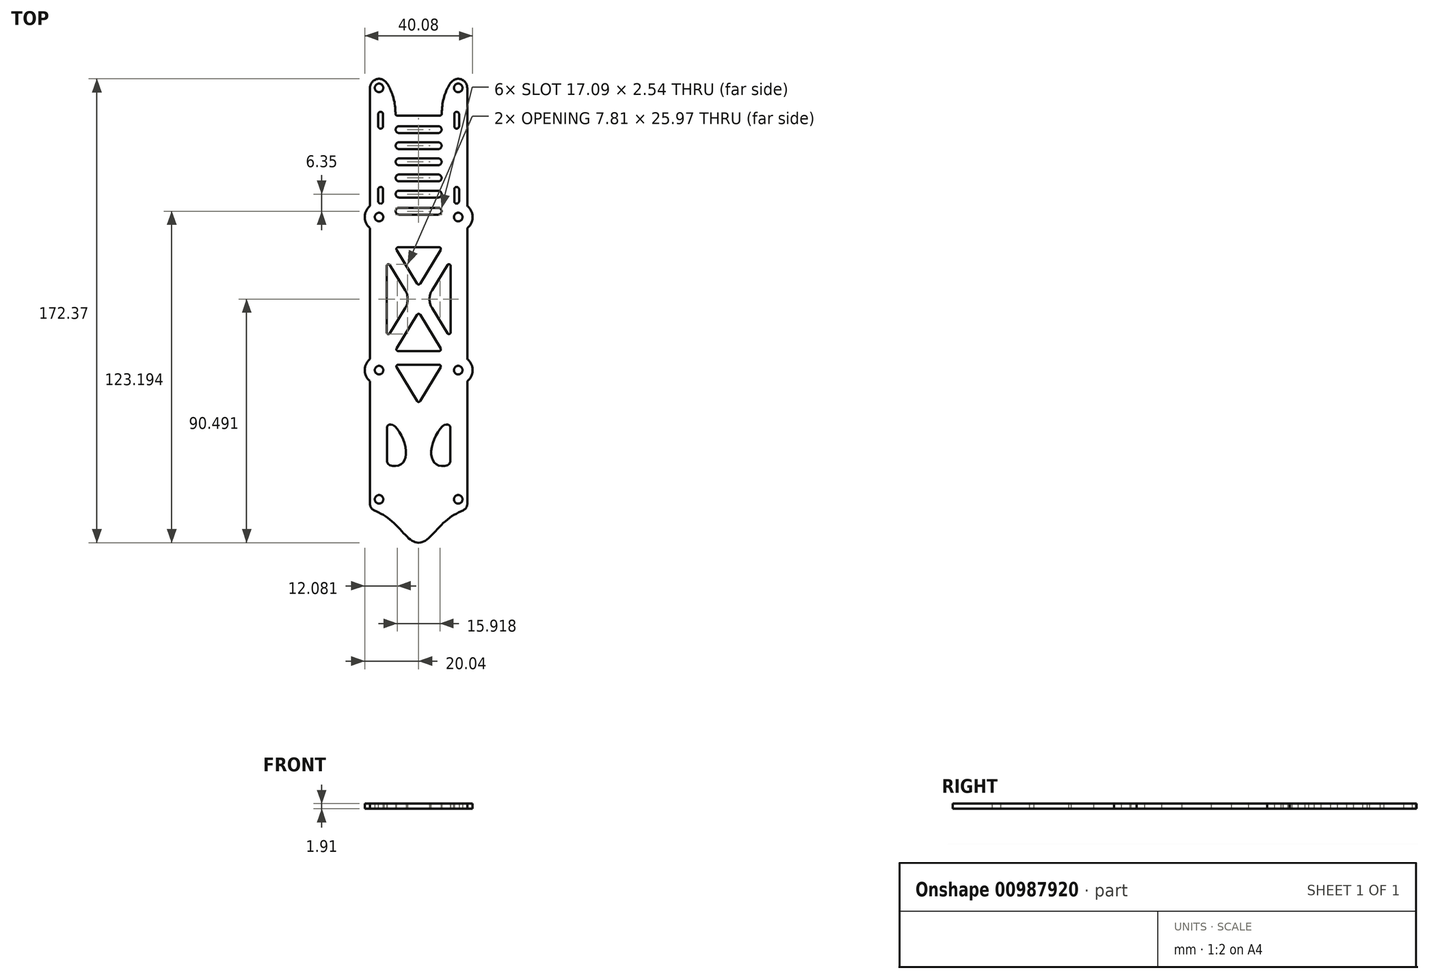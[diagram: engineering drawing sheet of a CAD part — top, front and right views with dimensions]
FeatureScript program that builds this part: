
annotation { "Feature Type Name" : "Feature", "Feature Type Description" : "" }
export const myFeature = defineFeature(function(context is Context, id is Id, definition is map)
    precondition{}
    {
        {
            var Q0;
            Q0=qCreatedBy(makeId("Top.planeOp"),FACE);
            var sketch = newSketch(context, id + "F0", { "sketchPlane" : qUnion([Q0])});
            skLineSegment(sketch, "E0.bottom", {"start": v(-8.07, 64.3) * mm, "end": v(0, 64.3) * mm});
            skLineSegment(sketch, "E0.left", {"start": v(-18.06, 64.3) * mm, "end": v(-18.06, 30.7) * mm});
            skLineSegment(sketch, "E1", {"start": v(-18.06, 64.3) * mm, "end": v(-18.06, 74.56) * mm});
            skArc(sketch, "E2", {"start": v(-12.9, 77.38) * mm, "mid": v(-16.31, 77.5) * mm, "end": v(-18.06, 74.56) * mm});
            skFitSpline(sketch, "E3", {"points": [v(-12.9, 77.38) * mm, v(-10.75, 74.43) * mm, v(-9.09, 69.74) * mm, v(-8.56, 64.3) * mm], "startDerivative": vector(10.32, -7.55) * mm, "endDerivative": vector(0.35, -10.82) * mm});
            skArc(sketch, "E4.filletArc", {"start": v(-8.58, 64.78) * mm, "mid": v(-8.42, 64.44) * mm, "end": v(-8.07, 64.3) * mm});
            skLineSegment(sketch, "E5", {"start": v(0, -94.46) * mm, "end": v(0, 99.76) * mm, "construction": true});
            skCircle(sketch, "E6", {"center": v(-14.7, 26.55) * mm, "radius": 1.59 * mm});
            skCircle(sketch, "E7", {"center": v(-14.7, -30.34) * mm, "radius": 1.59 * mm});
            skPoint(sketch, "E8.visualSharp", {"position": v(-18.06, -81.76) * mm});
            skCircle(sketch, "E9", {"center": v(-14.7, -78.35) * mm, "radius": 1.59 * mm});
            skFitSpline(sketch, "E10", {"points": [v(-18.06, -81.76) * mm, v(-10.46, -86.04) * mm, v(-3.87, -92.63) * mm, v(0, -94.46) * mm], "startDerivative": vector(21.5, -9.36) * mm, "endDerivative": vector(16.7, 0) * mm});
            skArc(sketch, "E11.filletArc", {"start": v(-18.06, -80.1) * mm, "mid": v(-17.65, -81.48) * mm, "end": v(-16.57, -82.42) * mm});
            skCircle(sketch, "E12", {"center": v(-14.7, 74.56) * mm, "radius": 1.59 * mm});
            skLineSegment(sketch, "E13.MirrorCS", {"start": v(8.07, 64.3) * mm, "end": v(0, 64.3) * mm});
            skArc(sketch, "E14.MirrorCS", {"start": v(8.58, 64.78) * mm, "mid": v(8.42, 64.44) * mm, "end": v(8.07, 64.3) * mm});
            skFitSpline(sketch, "E15.MirrorCS", {"points": [v(12.9, 77.38) * mm, v(10.75, 74.43) * mm, v(9.09, 69.74) * mm, v(8.56, 64.3) * mm], "startDerivative": vector(-10.32, -7.55) * mm, "endDerivative": vector(-0.35, -10.82) * mm});
            skArc(sketch, "E16.MirrorCS", {"start": v(12.9, 77.38) * mm, "mid": v(16.31, 77.5) * mm, "end": v(18.06, 74.56) * mm});
            skCircle(sketch, "E17.MirrorC", {"center": v(14.7, 74.56) * mm, "radius": 1.59 * mm});
            skLineSegment(sketch, "E18.MirrorCS", {"start": v(18.06, 64.3) * mm, "end": v(18.06, 74.56) * mm});
            skLineSegment(sketch, "E19.MirrorCS", {"start": v(18.06, 64.3) * mm, "end": v(18.06, 30.7) * mm});
            skCircle(sketch, "E20.MirrorC", {"center": v(14.7, 26.55) * mm, "radius": 1.59 * mm});
            skCircle(sketch, "E21.MirrorC", {"center": v(14.7, -30.34) * mm, "radius": 1.59 * mm});
            skCircle(sketch, "E22.MirrorC", {"center": v(14.7, -78.35) * mm, "radius": 1.59 * mm});
            skArc(sketch, "E23.MirrorCS", {"start": v(18.06, -80.1) * mm, "mid": v(17.65, -81.48) * mm, "end": v(16.57, -82.42) * mm});
            skFitSpline(sketch, "E24.MirrorCS", {"points": [v(18.06, -81.76) * mm, v(10.46, -86.04) * mm, v(3.87, -92.63) * mm, v(0, -94.46) * mm], "startDerivative": vector(-21.5, -9.36) * mm, "endDerivative": vector(-16.7, 0) * mm});
            skLineSegment(sketch, "E25", {"start": v(-11.86, 8.38) * mm, "end": v(-11.86, -16.32) * mm});
            skLineSegment(sketch, "E26", {"start": v(-10.7, -16.65) * mm, "end": v(-4.98, -7.27) * mm});
            skLineSegment(sketch, "E27", {"start": v(-4.98, -0.67) * mm, "end": v(-10.7, 8.71) * mm});
            skLineSegment(sketch, "E28", {"start": v(-0.54, -9.74) * mm, "end": v(-8.18, -22.3) * mm});
            skLineSegment(sketch, "E29", {"start": v(-7.64, -23.25) * mm, "end": v(0, -23.25) * mm});
            skLineSegment(sketch, "E30", {"start": v(-2.97, -3.97) * mm, "end": v(7.15, -3.97) * mm, "construction": true});
            skLineSegment(sketch, "E31.MirrorCS", {"start": v(-0.54, 1.8) * mm, "end": v(-8.18, 14.36) * mm});
            skLineSegment(sketch, "E32.MirrorCS", {"start": v(-7.64, 15.32) * mm, "end": v(0, 15.32) * mm});
            skPoint(sketch, "E33.visualSharp", {"position": v(-2.97, -3.97) * mm});
            skArc(sketch, "E33.filletArc", {"start": v(-4.98, -7.27) * mm, "mid": v(-4.06, -3.97) * mm, "end": v(-4.98, -0.67) * mm});
            skPoint(sketch, "E34.visualSharp", {"position": v(-11.86, 10.64) * mm});
            skArc(sketch, "E34.filletArc", {"start": v(-10.7, 8.71) * mm, "mid": v(-11.4, 9) * mm, "end": v(-11.86, 8.38) * mm});
            skPoint(sketch, "E35.visualSharp", {"position": v(-11.86, -18.57) * mm});
            skArc(sketch, "E35.filletArc", {"start": v(-11.86, -16.32) * mm, "mid": v(-11.4, -16.93) * mm, "end": v(-10.7, -16.65) * mm});
            skPoint(sketch, "E36.visualSharp", {"position": v(-8.76, 15.32) * mm});
            skArc(sketch, "E36.filletArc", {"start": v(-7.64, 15.32) * mm, "mid": v(-8.19, 15) * mm, "end": v(-8.18, 14.36) * mm});
            skPoint(sketch, "E37.visualSharp", {"position": v(-8.76, -23.25) * mm});
            skArc(sketch, "E37.filletArc", {"start": v(-8.18, -22.3) * mm, "mid": v(-8.19, -22.93) * mm, "end": v(-7.64, -23.25) * mm});
            skLineSegment(sketch, "E38.MirrorCS", {"start": v(7.64, 15.32) * mm, "end": v(0, 15.32) * mm});
            skLineSegment(sketch, "E39.MirrorCS", {"start": v(0.54, 1.8) * mm, "end": v(8.18, 14.36) * mm});
            skArc(sketch, "E40.MirrorCS", {"start": v(7.64, 15.32) * mm, "mid": v(8.19, 15) * mm, "end": v(8.18, 14.36) * mm});
            skLineSegment(sketch, "E41.MirrorCS", {"start": v(4.98, -0.67) * mm, "end": v(10.7, 8.71) * mm});
            skLineSegment(sketch, "E42.MirrorCS", {"start": v(11.86, 8.38) * mm, "end": v(11.86, -16.32) * mm});
            skArc(sketch, "E43.MirrorCS", {"start": v(10.7, 8.71) * mm, "mid": v(11.4, 9) * mm, "end": v(11.86, 8.38) * mm});
            skLineSegment(sketch, "E44.MirrorCS", {"start": v(10.7, -16.65) * mm, "end": v(4.98, -7.27) * mm});
            skArc(sketch, "E45.MirrorCS", {"start": v(11.86, -16.32) * mm, "mid": v(11.4, -16.93) * mm, "end": v(10.7, -16.65) * mm});
            skLineSegment(sketch, "E46.MirrorCS", {"start": v(0.54, -9.74) * mm, "end": v(8.18, -22.3) * mm});
            skLineSegment(sketch, "E47.MirrorCS", {"start": v(7.64, -23.25) * mm, "end": v(0, -23.25) * mm});
            skArc(sketch, "E48.MirrorCS", {"start": v(4.98, -7.27) * mm, "mid": v(4.06, -3.97) * mm, "end": v(4.98, -0.67) * mm});
            skArc(sketch, "E49.MirrorCS", {"start": v(8.18, -22.3) * mm, "mid": v(8.19, -22.93) * mm, "end": v(7.64, -23.25) * mm});
            skPoint(sketch, "E50.visualSharp", {"position": v(0, 0.92) * mm});
            skArc(sketch, "E50.filletArc", {"start": v(-0.54, 1.8) * mm, "mid": v(0, 1.5) * mm, "end": v(0.54, 1.8) * mm});
            skPoint(sketch, "E51.visualSharp", {"position": v(0, -8.86) * mm});
            skArc(sketch, "E51.filletArc", {"start": v(0.54, -9.74) * mm, "mid": v(0, -9.44) * mm, "end": v(-0.54, -9.74) * mm});
            skArc(sketch, "E52", {"start": v(-18.06, 30.7) * mm, "mid": v(-20.04, 26.55) * mm, "end": v(-18.06, 22.41) * mm});
            skArc(sketch, "E53", {"start": v(18.06, 22.41) * mm, "mid": v(20.04, 26.55) * mm, "end": v(18.06, 30.7) * mm});
            skArc(sketch, "E54", {"start": v(18.06, -34.48) * mm, "mid": v(20.04, -30.34) * mm, "end": v(18.06, -26.2) * mm});
            skArc(sketch, "E55", {"start": v(-18.06, -26.2) * mm, "mid": v(-20.04, -30.34) * mm, "end": v(-18.06, -34.48) * mm});
            skLineSegment(sketch, "E56.trimOffspring", {"start": v(18.06, -34.48) * mm, "end": v(18.06, -80.1) * mm});
            skLineSegment(sketch, "E57.trimOffspring", {"start": v(-18.06, -34.48) * mm, "end": v(-18.06, -80.1) * mm});
            skLineSegment(sketch, "E58.trimOffspring", {"start": v(18.06, 22.41) * mm, "end": v(18.06, -26.2) * mm});
            skLineSegment(sketch, "E59.trimOffspring", {"start": v(-18.06, 22.41) * mm, "end": v(-18.06, -26.2) * mm});
            skLineSegment(sketch, "E60", {"start": v(-11.72, -64.38) * mm, "end": v(-11.72, -51.49) * mm});
            skFitSpline(sketch, "E61", {"points": [v(-11.72, -51.49) * mm, v(-9.93, -50.58) * mm, v(-4.83, -59.28) * mm, v(-7.13, -65.64) * mm, v(-11.72, -64.38) * mm], "startDerivative": vector(1.58, 12.9) * mm, "endDerivative": vector(-1.26, 20.83) * mm});
            skFitSpline(sketch, "E62.MirrorCS", {"points": [v(11.72, -51.49) * mm, v(9.93, -50.58) * mm, v(4.83, -59.28) * mm, v(7.13, -65.64) * mm, v(11.72, -64.38) * mm], "startDerivative": vector(-1.58, 12.9) * mm, "endDerivative": vector(1.26, 20.83) * mm});
            skLineSegment(sketch, "E63.MirrorCS", {"start": v(11.72, -64.38) * mm, "end": v(11.72, -51.49) * mm});
            skArc(sketch, "E64", {"start": v(-13.23, 64.75) * mm, "mid": v(-14.12, 65.64) * mm, "end": v(-15.01, 64.75) * mm});
            skArc(sketch, "E65", {"start": v(-15.01, 60.3) * mm, "mid": v(-14.12, 59.42) * mm, "end": v(-13.23, 60.3) * mm});
            skArc(sketch, "E66", {"start": v(-13.23, 36.86) * mm, "mid": v(-14.12, 37.75) * mm, "end": v(-15.01, 36.86) * mm});
            skArc(sketch, "E67", {"start": v(-15.01, 32.42) * mm, "mid": v(-14.12, 31.53) * mm, "end": v(-13.23, 32.42) * mm});
            skLineSegment(sketch, "E68", {"start": v(-15.01, 64.75) * mm, "end": v(-15.01, 60.3) * mm});
            skLineSegment(sketch, "E69", {"start": v(-13.23, 64.75) * mm, "end": v(-13.23, 60.3) * mm});
            skLineSegment(sketch, "E70", {"start": v(-15.01, 36.86) * mm, "end": v(-15.01, 32.42) * mm});
            skLineSegment(sketch, "E71", {"start": v(-13.23, 36.86) * mm, "end": v(-13.23, 32.42) * mm});
            skArc(sketch, "E72.MirrorCS", {"start": v(13.23, 64.75) * mm, "mid": v(14.12, 65.64) * mm, "end": v(15.01, 64.75) * mm});
            skLineSegment(sketch, "E73.MirrorCS", {"start": v(15.01, 64.75) * mm, "end": v(15.01, 60.3) * mm});
            skArc(sketch, "E74.MirrorCS", {"start": v(15.01, 60.3) * mm, "mid": v(14.12, 59.42) * mm, "end": v(13.23, 60.3) * mm});
            skLineSegment(sketch, "E75.MirrorCS", {"start": v(13.23, 64.75) * mm, "end": v(13.23, 60.3) * mm});
            skArc(sketch, "E76.MirrorCS", {"start": v(13.23, 36.86) * mm, "mid": v(14.12, 37.75) * mm, "end": v(15.01, 36.86) * mm});
            skLineSegment(sketch, "E77.MirrorCS", {"start": v(15.01, 36.86) * mm, "end": v(15.01, 32.42) * mm});
            skLineSegment(sketch, "E78.MirrorCS", {"start": v(13.23, 36.86) * mm, "end": v(13.23, 32.42) * mm});
            skArc(sketch, "E79.MirrorCS", {"start": v(15.01, 32.42) * mm, "mid": v(14.12, 31.53) * mm, "end": v(13.23, 32.42) * mm});
            skArc(sketch, "E80", {"start": v(-7.28, 36.35) * mm, "mid": v(-8.55, 35.08) * mm, "end": v(-7.28, 33.81) * mm});
            skLineSegment(sketch, "E81", {"start": v(-7.28, 36.35) * mm, "end": v(0, 36.35) * mm});
            skLineSegment(sketch, "E82", {"start": v(0, 33.81) * mm, "end": v(-7.28, 33.81) * mm});
            skLineSegment(sketch, "E83.MirrorCS", {"start": v(7.28, 36.35) * mm, "end": v(0, 36.35) * mm});
            skLineSegment(sketch, "E84.MirrorCS", {"start": v(0, 33.81) * mm, "end": v(7.28, 33.81) * mm});
            skArc(sketch, "E85.MirrorCS", {"start": v(7.28, 36.35) * mm, "mid": v(8.55, 35.08) * mm, "end": v(7.28, 33.81) * mm});
            skLineSegment(sketch, "E86", {"start": v(-9.8, -25.8) * mm, "end": v(9.93, -25.8) * mm, "construction": true});
            skLineSegment(sketch, "E87.MirrorCS", {"start": v(7.64, -28.33) * mm, "end": v(0, -28.33) * mm});
            skLineSegment(sketch, "E88.MirrorCS", {"start": v(-7.64, -28.33) * mm, "end": v(0, -28.33) * mm});
            skLineSegment(sketch, "E89.MirrorCS", {"start": v(0.54, -41.84) * mm, "end": v(8.18, -29.3) * mm});
            skLineSegment(sketch, "E90.MirrorCS", {"start": v(-0.54, -41.84) * mm, "end": v(-8.18, -29.3) * mm});
            skArc(sketch, "E91.MirrorCS", {"start": v(0.54, -41.84) * mm, "mid": v(0, -42.15) * mm, "end": v(-0.54, -41.84) * mm});
            skArc(sketch, "E92.MirrorCS", {"start": v(8.18, -29.3) * mm, "mid": v(8.19, -28.66) * mm, "end": v(7.64, -28.33) * mm});
            skArc(sketch, "E93.MirrorCS", {"start": v(-8.18, -29.3) * mm, "mid": v(-8.19, -28.66) * mm, "end": v(-7.64, -28.33) * mm});
            skLineSegment(sketch, "E94.1.0.0", {"start": v(7.28, 42.35) * mm, "end": v(0, 42.35) * mm});
            skLineSegment(sketch, "E94.1.0.1", {"start": v(0, 39.8) * mm, "end": v(7.28, 39.8) * mm});
            skArc(sketch, "E94.1.0.2", {"start": v(7.28, 42.35) * mm, "mid": v(8.55, 41.08) * mm, "end": v(7.28, 39.8) * mm});
            skLineSegment(sketch, "E94.1.0.3", {"start": v(-7.28, 42.35) * mm, "end": v(0, 42.35) * mm});
            skLineSegment(sketch, "E94.1.0.4", {"start": v(0, 39.8) * mm, "end": v(-7.28, 39.8) * mm});
            skArc(sketch, "E94.1.0.5", {"start": v(-7.28, 42.35) * mm, "mid": v(-8.55, 41.08) * mm, "end": v(-7.28, 39.8) * mm});
            skLineSegment(sketch, "E94.2.0.0", {"start": v(7.28, 48.34) * mm, "end": v(0, 48.34) * mm});
            skLineSegment(sketch, "E94.2.0.1", {"start": v(0, 45.8) * mm, "end": v(7.28, 45.8) * mm});
            skArc(sketch, "E94.2.0.2", {"start": v(7.28, 48.34) * mm, "mid": v(8.55, 47.07) * mm, "end": v(7.28, 45.8) * mm});
            skLineSegment(sketch, "E94.2.0.3", {"start": v(-7.28, 48.34) * mm, "end": v(0, 48.34) * mm});
            skLineSegment(sketch, "E94.2.0.4", {"start": v(0, 45.8) * mm, "end": v(-7.28, 45.8) * mm});
            skArc(sketch, "E94.2.0.5", {"start": v(-7.28, 48.34) * mm, "mid": v(-8.55, 47.07) * mm, "end": v(-7.28, 45.8) * mm});
            skLineSegment(sketch, "E94.3.0.0", {"start": v(7.28, 54.34) * mm, "end": v(0, 54.34) * mm});
            skLineSegment(sketch, "E94.3.0.1", {"start": v(0, 51.8) * mm, "end": v(7.28, 51.8) * mm});
            skArc(sketch, "E94.3.0.2", {"start": v(7.28, 54.34) * mm, "mid": v(8.55, 53.07) * mm, "end": v(7.28, 51.8) * mm});
            skLineSegment(sketch, "E94.3.0.3", {"start": v(-7.28, 54.34) * mm, "end": v(0, 54.34) * mm});
            skLineSegment(sketch, "E94.3.0.4", {"start": v(0, 51.8) * mm, "end": v(-7.28, 51.8) * mm});
            skArc(sketch, "E94.3.0.5", {"start": v(-7.28, 54.34) * mm, "mid": v(-8.55, 53.07) * mm, "end": v(-7.28, 51.8) * mm});
            skLineSegment(sketch, "E94.direction1", {"start": v(0, 36.35) * mm, "end": v(0, 42.35) * mm, "construction": true});
            skLineSegment(sketch, "E95.0.4.0", {"start": v(7.28, 60.33) * mm, "end": v(0, 60.33) * mm});
            skLineSegment(sketch, "E95.3.4.0", {"start": v(0, 57.8) * mm, "end": v(7.28, 57.8) * mm});
            skArc(sketch, "E95.6.4.0", {"start": v(7.28, 60.33) * mm, "mid": v(8.55, 59.06) * mm, "end": v(7.28, 57.8) * mm});
            skLineSegment(sketch, "E95.10.4.0", {"start": v(-7.28, 60.33) * mm, "end": v(0, 60.33) * mm});
            skLineSegment(sketch, "E95.13.4.0", {"start": v(0, 57.8) * mm, "end": v(-7.28, 57.8) * mm});
            skArc(sketch, "E95.16.4.0", {"start": v(-7.28, 60.33) * mm, "mid": v(-8.55, 59.06) * mm, "end": v(-7.28, 57.8) * mm});
            skLineSegment(sketch, "E96", {"start": v(-7.13, 31.9) * mm, "end": v(7.15, 31.9) * mm, "construction": true});
            skLineSegment(sketch, "E97.MirrorCS", {"start": v(0, 30) * mm, "end": v(7.28, 30) * mm});
            skLineSegment(sketch, "E98.MirrorCS", {"start": v(7.28, 27.46) * mm, "end": v(0, 27.46) * mm});
            skArc(sketch, "E99.MirrorCS", {"start": v(7.28, 27.46) * mm, "mid": v(8.55, 28.73) * mm, "end": v(7.28, 30) * mm});
            skLineSegment(sketch, "E100.MirrorCS", {"start": v(-7.28, 27.46) * mm, "end": v(0, 27.46) * mm});
            skLineSegment(sketch, "E101.MirrorCS", {"start": v(0, 30) * mm, "end": v(-7.28, 30) * mm});
            skArc(sketch, "E102.MirrorCS", {"start": v(-7.28, 27.46) * mm, "mid": v(-8.55, 28.73) * mm, "end": v(-7.28, 30) * mm});
            skLineSegment(sketch, "E103", {"start": v(20.05, 64.75) * mm, "end": v(6.6, 64.75) * mm, "construction": true});
            skLineSegment(sketch, "E104", {"start": v(-20.82, 64.75) * mm, "end": v(-2.43, 64.75) * mm, "construction": true});
            skSolve(sketch);
        }
        {
            var Q0;
            Q0 = qSketchRegion(id + "F0", true);
            extrude(context, id + "F1", {"entities" : qUnion([Q0]), "depth" : 1.9 * mm, "offsetDistance" : 25.4 * mm});
        }
    });
